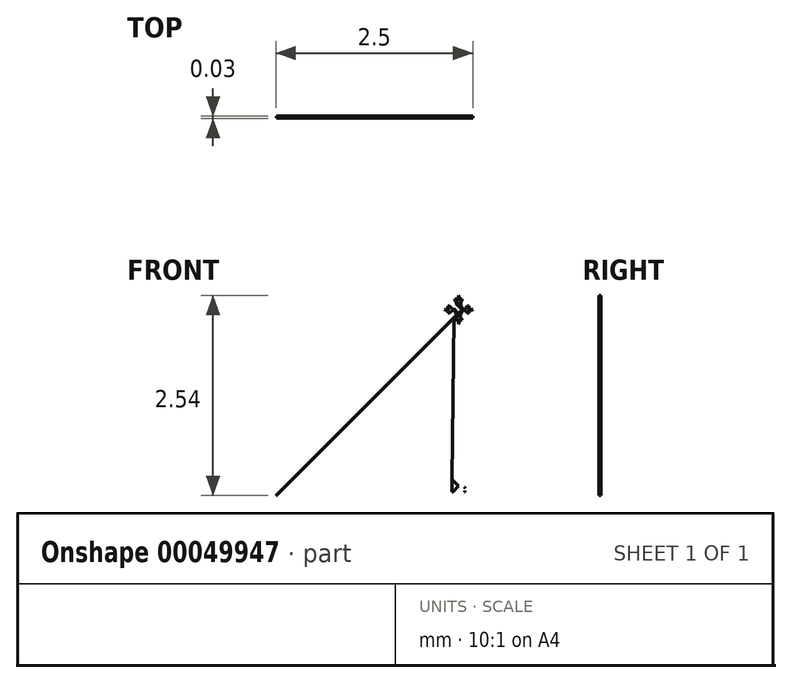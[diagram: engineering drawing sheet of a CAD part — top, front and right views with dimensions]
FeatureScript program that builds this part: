
annotation { "Feature Type Name" : "Feature", "Feature Type Description" : "" }
export const myFeature = defineFeature(function(context is Context, id is Id, definition is map)
    precondition{}
    {
        {
            var Q0;
            Q0=qCreatedBy(makeId("Front.planeOp"),FACE);
            var sketch = newSketch(context, id + "F0", { "sketchPlane" : qUnion([Q0])});
            skLineSegment(sketch, "E0", {"start": v(0, 0) * mm, "end": v(5.08, 0) * mm, "construction": true});
            skLineSegment(sketch, "E1", {"start": v(5.08, 0) * mm, "end": v(5.08, 5.08) * mm, "construction": true});
            skLineSegment(sketch, "E2", {"start": v(5.08, 5.08) * mm, "end": v(0, 5.08) * mm, "construction": true});
            skLineSegment(sketch, "E3", {"start": v(0, 5.08) * mm, "end": v(0, 0) * mm, "construction": true});
            skLineSegment(sketch, "E4", {"start": v(0, 2.54) * mm, "end": v(5.08, 2.54) * mm, "construction": true});
            skLineSegment(sketch, "E5", {"start": v(5.08, 2.54) * mm, "end": v(2.54, 5.08) * mm, "construction": true});
            skLineSegment(sketch, "E6", {"start": v(2.54, 5.08) * mm, "end": v(2.54, 0) * mm, "construction": true});
            skLineSegment(sketch, "E7", {"start": v(2.54, 0) * mm, "end": v(0, 2.54) * mm, "construction": true});
            skLineSegment(sketch, "E8", {"start": v(2.54, 5.08) * mm, "end": v(0, 2.54) * mm, "construction": true});
            skLineSegment(sketch, "E9", {"start": v(2.54, 0) * mm, "end": v(5.08, 2.54) * mm, "construction": true});
            skCircle(sketch, "E10.cCircle", {"center": v(2.54, 2.54) * mm, "radius": 0.05 * mm, "construction": true});
            skLineSegment(sketch, "E10.0", {"start": v(2.57, 2.49) * mm, "end": v(2.51, 2.49) * mm});
            skLineSegment(sketch, "E10.1", {"start": v(2.51, 2.49) * mm, "end": v(2.48, 2.54) * mm});
            skLineSegment(sketch, "E10.2", {"start": v(2.48, 2.54) * mm, "end": v(2.51, 2.6) * mm});
            skLineSegment(sketch, "E10.3", {"start": v(2.51, 2.6) * mm, "end": v(2.57, 2.6) * mm});
            skLineSegment(sketch, "E10.4", {"start": v(2.57, 2.6) * mm, "end": v(2.6, 2.54) * mm});
            skLineSegment(sketch, "E10.5", {"start": v(2.6, 2.54) * mm, "end": v(2.57, 2.49) * mm});
            skPoint(sketch, "E10.0.midPoint", {"position": v(2.54, 2.49) * mm});
            skLineSegment(sketch, "E11", {"start": v(2.54, 2.54) * mm, "end": v(2.6, 2.54) * mm});
            skLineSegment(sketch, "E12", {"start": v(2.54, 2.54) * mm, "end": v(2.54, 2.54) * mm});
            skLineSegment(sketch, "E13", {"start": v(5.08, 0.25) * mm, "end": v(5.08, 0.26) * mm});
            skLineSegment(sketch, "E14", {"start": v(0.26, 5.08) * mm, "end": v(0.25, 5.08) * mm});
            skLineSegment(sketch, "E15", {"start": v(0, 0.25) * mm, "end": v(0, 0.26) * mm});
            skLineSegment(sketch, "E16", {"start": v(0.26, 0) * mm, "end": v(0.25, 0) * mm});
            skLineSegment(sketch, "E17", {"start": v(2.51, 2.6) * mm, "end": v(2.51, 2.62) * mm, "construction": true});
            skLineSegment(sketch, "E18", {"start": v(2.51, 2.62) * mm, "end": v(2.54, 2.62) * mm, "construction": true});
            skLineSegment(sketch, "E19", {"start": v(2.54, 2.6) * mm, "end": v(2.51, 2.62) * mm});
            skLineSegment(sketch, "E20", {"start": v(2.51, 2.62) * mm, "end": v(2.52, 2.62) * mm});
            skLineSegment(sketch, "E21", {"start": v(2.51, 2.62) * mm, "end": v(2.51, 2.6) * mm});
            skLineSegment(sketch, "E22", {"start": v(2.52, 2.62) * mm, "end": v(2.54, 2.6) * mm});
            skLineSegment(sketch, "E23", {"start": v(2.51, 2.6) * mm, "end": v(2.53, 2.6) * mm});
            skLineSegment(sketch, "E24", {"start": v(2.57, 2.6) * mm, "end": v(2.57, 2.62) * mm, "construction": true});
            skLineSegment(sketch, "E25", {"start": v(2.57, 2.62) * mm, "end": v(0.26, 2.62) * mm, "construction": true});
            skLineSegment(sketch, "E26", {"start": v(2.57, 2.62) * mm, "end": v(2.54, 2.6) * mm});
            skLineSegment(sketch, "E27", {"start": v(2.57, 2.62) * mm, "end": v(2.56, 2.62) * mm});
            skLineSegment(sketch, "E28", {"start": v(2.57, 2.62) * mm, "end": v(2.57, 2.6) * mm});
            skLineSegment(sketch, "E29", {"start": v(2.54, 2.62) * mm, "end": v(2.54, 2.6) * mm});
            skLineSegment(sketch, "E30", {"start": v(2.57, 2.6) * mm, "end": v(2.56, 2.62) * mm});
            skLineSegment(sketch, "E31", {"start": v(2.56, 2.62) * mm, "end": v(2.54, 2.6) * mm});
            skLineSegment(sketch, "E32", {"start": v(2.57, 2.6) * mm, "end": v(2.55, 2.6) * mm});
            skLineSegment(sketch, "E33", {"start": v(0.22, 0.18) * mm, "end": v(0.25, 0.18) * mm, "construction": true});
            skLineSegment(sketch, "E34", {"start": v(2.57, 2.46) * mm, "end": v(2.54, 2.49) * mm});
            skLineSegment(sketch, "E35", {"start": v(2.54, 2.49) * mm, "end": v(0.22, 0.18) * mm});
            skLineSegment(sketch, "E36", {"start": v(0.22, 0.18) * mm, "end": v(0.22, 0.19) * mm});
            skLineSegment(sketch, "E37", {"start": v(0.22, 0.18) * mm, "end": v(0.23, 0.18) * mm});
            skLineSegment(sketch, "E38", {"start": v(0.23, 0.18) * mm, "end": v(0.22, 0.19) * mm});
            skLineSegment(sketch, "E39", {"start": v(0.22, 0.19) * mm, "end": v(2.53, 2.49) * mm});
            skLineSegment(sketch, "E40", {"start": v(0.23, 0.18) * mm, "end": v(0.25, 0.2) * mm});
            skLineSegment(sketch, "E41", {"start": v(2.57, 2.46) * mm, "end": v(2.57, 2.47) * mm});
            skLineSegment(sketch, "E42", {"start": v(2.57, 2.46) * mm, "end": v(2.56, 2.46) * mm});
            skLineSegment(sketch, "E43", {"start": v(2.56, 2.46) * mm, "end": v(2.54, 2.48) * mm});
            skLineSegment(sketch, "E44", {"start": v(2.57, 2.47) * mm, "end": v(2.55, 2.49) * mm});
            skLineSegment(sketch, "E45", {"start": v(2.54, 2.54) * mm, "end": v(2.5, 2.54) * mm});
            skCircle(sketch, "E46.cCircle", {"center": v(2.54, 2.54) * mm, "radius": 0.04 * mm, "construction": true});
            skLineSegment(sketch, "E46.0", {"start": v(2.5, 2.52) * mm, "end": v(2.5, 2.56) * mm});
            skLineSegment(sketch, "E46.1", {"start": v(2.5, 2.56) * mm, "end": v(2.54, 2.58) * mm});
            skLineSegment(sketch, "E46.2", {"start": v(2.54, 2.58) * mm, "end": v(2.58, 2.56) * mm});
            skLineSegment(sketch, "E46.3", {"start": v(2.58, 2.56) * mm, "end": v(2.58, 2.52) * mm});
            skLineSegment(sketch, "E46.4", {"start": v(2.58, 2.52) * mm, "end": v(2.54, 2.5) * mm});
            skLineSegment(sketch, "E46.5", {"start": v(2.54, 2.5) * mm, "end": v(2.5, 2.52) * mm});
            skPoint(sketch, "E46.0.midPoint", {"position": v(2.5, 2.54) * mm});
            skLineSegment(sketch, "E47", {"start": v(2.6, 0.26) * mm, "end": v(2.6, 2.54) * mm});
            skLineSegment(sketch, "E48", {"start": v(2.6, 0.26) * mm, "end": v(2.6, 0.25) * mm});
            skLineSegment(sketch, "E49", {"start": v(2.6, 0.25) * mm, "end": v(2.6, 0.22) * mm, "construction": true});
            skLineSegment(sketch, "E50", {"start": v(2.6, 0.22) * mm, "end": v(2.62, 0.22) * mm, "construction": true});
            skLineSegment(sketch, "E51", {"start": v(2.62, 0.22) * mm, "end": v(2.62, 0.25) * mm, "construction": true});
            skLineSegment(sketch, "E52", {"start": v(2.6, 0.25) * mm, "end": v(2.62, 0.22) * mm});
            skLineSegment(sketch, "E53", {"start": v(2.62, 0.22) * mm, "end": v(2.62, 0.23) * mm});
            skLineSegment(sketch, "E54", {"start": v(2.62, 0.22) * mm, "end": v(2.61, 0.22) * mm});
            skLineSegment(sketch, "E55", {"start": v(2.61, 0.22) * mm, "end": v(2.62, 0.23) * mm});
            skLineSegment(sketch, "E56", {"start": v(2.62, 0.23) * mm, "end": v(2.6, 0.25) * mm});
            skLineSegment(sketch, "E57", {"start": v(2.61, 0.22) * mm, "end": v(1.76, 1.08) * mm});
            skLineSegment(sketch, "E58", {"start": v(2.6, 0.26) * mm, "end": v(2.6, 0.28) * mm, "construction": true});
            skLineSegment(sketch, "E59", {"start": v(2.6, 0.28) * mm, "end": v(2.62, 0.28) * mm, "construction": true});
            skLineSegment(sketch, "E60", {"start": v(2.62, 0.28) * mm, "end": v(2.62, 0.26) * mm, "construction": true});
            skLineSegment(sketch, "E61", {"start": v(2.6, 0.26) * mm, "end": v(2.62, 0.28) * mm});
            skLineSegment(sketch, "E62", {"start": v(2.62, 0.27) * mm, "end": v(2.62, 0.28) * mm});
            skLineSegment(sketch, "E63", {"start": v(2.62, 0.28) * mm, "end": v(2.61, 0.28) * mm});
            skLineSegment(sketch, "E64", {"start": v(2.61, 0.28) * mm, "end": v(2.62, 0.27) * mm});
            skLineSegment(sketch, "E65", {"start": v(3.43, 1.1) * mm, "end": v(2.61, 0.28) * mm});
            skLineSegment(sketch, "E66", {"start": v(2.62, 0.27) * mm, "end": v(2.6, 0.26) * mm});
            skLineSegment(sketch, "E67", {"start": v(2.48, 2.54) * mm, "end": v(2.48, 2.54) * mm});
            skLineSegment(sketch, "E68", {"start": v(2.48, 0.28) * mm, "end": v(2.48, 2.54) * mm, "construction": true});
            skLineSegment(sketch, "E69", {"start": v(2.48, 0.28) * mm, "end": v(2.46, 0.28) * mm, "construction": true});
            skLineSegment(sketch, "E70", {"start": v(2.46, 0.28) * mm, "end": v(2.46, 0.26) * mm, "construction": true});
            skLineSegment(sketch, "E71", {"start": v(2.48, 2.54) * mm, "end": v(2.46, 0.28) * mm});
            skLineSegment(sketch, "E72", {"start": v(2.46, 0.28) * mm, "end": v(2.47, 0.28) * mm});
            skLineSegment(sketch, "E73", {"start": v(2.46, 0.28) * mm, "end": v(2.46, 0.27) * mm});
            skLineSegment(sketch, "E74", {"start": v(2.46, 0.27) * mm, "end": v(2.47, 0.28) * mm});
            skLineSegment(sketch, "E75", {"start": v(2.46, 0.27) * mm, "end": v(2.47, 0.26) * mm});
            skLineSegment(sketch, "E76", {"start": v(1.65, 1.1) * mm, "end": v(2.47, 0.28) * mm});
            skLineSegment(sketch, "E77", {"start": v(2.48, 2.54) * mm, "end": v(2.48, 0.22) * mm, "construction": true});
            skLineSegment(sketch, "E78", {"start": v(2.48, 0.22) * mm, "end": v(2.46, 0.22) * mm, "construction": true});
            skLineSegment(sketch, "E79", {"start": v(2.46, 0.22) * mm, "end": v(2.46, 0.25) * mm, "construction": true});
            skLineSegment(sketch, "E80", {"start": v(2.46, 0.22) * mm, "end": v(2.48, 2.54) * mm});
            skLineSegment(sketch, "E81", {"start": v(2.46, 0.22) * mm, "end": v(2.47, 0.22) * mm});
            skLineSegment(sketch, "E82", {"start": v(2.47, 0.22) * mm, "end": v(2.46, 0.23) * mm});
            skLineSegment(sketch, "E83", {"start": v(2.46, 0.23) * mm, "end": v(2.46, 0.22) * mm});
            skLineSegment(sketch, "E84", {"start": v(2.46, 0.23) * mm, "end": v(2.47, 0.25) * mm});
            skLineSegment(sketch, "E85", {"start": v(2.47, 0.22) * mm, "end": v(3.32, 1.08) * mm});
            skLineSegment(sketch, "E86", {"start": v(2.54, 2.54) * mm, "end": v(2.36, 2.54) * mm});
            skLineSegment(sketch, "E87", {"start": v(2.36, 2.54) * mm, "end": v(2.36, 2.54) * mm});
            skLineSegment(sketch, "E88", {"start": v(2.54, 2.54) * mm, "end": v(2.72, 2.54) * mm});
            skLineSegment(sketch, "E89", {"start": v(2.72, 2.54) * mm, "end": v(2.72, 2.54) * mm});
            skLineSegment(sketch, "E90", {"start": v(2.54, 2.54) * mm, "end": v(2.54, 2.72) * mm});
            skLineSegment(sketch, "E91", {"start": v(2.54, 2.72) * mm, "end": v(2.54, 2.72) * mm});
            skLineSegment(sketch, "E92", {"start": v(2.54, 2.54) * mm, "end": v(2.54, 2.36) * mm});
            skLineSegment(sketch, "E93", {"start": v(2.54, 2.36) * mm, "end": v(2.54, 2.36) * mm});
            skLineSegment(sketch, "E94", {"start": v(2.63, 2.54) * mm, "end": v(2.63, 2.58) * mm});
            skLineSegment(sketch, "E95", {"start": v(2.63, 2.58) * mm, "end": v(2.67, 2.58) * mm, "construction": true});
            skLineSegment(sketch, "E96", {"start": v(2.67, 2.58) * mm, "end": v(2.67, 2.54) * mm, "construction": true});
            skLineSegment(sketch, "E97", {"start": v(2.67, 2.58) * mm, "end": v(2.63, 2.54) * mm});
            skLineSegment(sketch, "E98", {"start": v(2.67, 2.58) * mm, "end": v(2.67, 2.56) * mm});
            skLineSegment(sketch, "E99", {"start": v(2.67, 2.56) * mm, "end": v(2.65, 2.58) * mm});
            skLineSegment(sketch, "E100", {"start": v(2.65, 2.58) * mm, "end": v(2.67, 2.58) * mm});
            skLineSegment(sketch, "E101", {"start": v(2.65, 2.58) * mm, "end": v(2.61, 2.54) * mm});
            skLineSegment(sketch, "E102", {"start": v(2.67, 2.56) * mm, "end": v(2.65, 2.54) * mm});
            skLineSegment(sketch, "E103", {"start": v(2.63, 2.54) * mm, "end": v(2.63, 2.5) * mm});
            skLineSegment(sketch, "E104", {"start": v(2.63, 2.5) * mm, "end": v(2.67, 2.5) * mm, "construction": true});
            skLineSegment(sketch, "E105", {"start": v(2.67, 2.5) * mm, "end": v(2.67, 2.54) * mm, "construction": true});
            skLineSegment(sketch, "E106", {"start": v(2.63, 2.54) * mm, "end": v(2.67, 2.5) * mm});
            skLineSegment(sketch, "E107", {"start": v(2.67, 2.52) * mm, "end": v(2.67, 2.5) * mm});
            skLineSegment(sketch, "E108", {"start": v(2.67, 2.52) * mm, "end": v(2.65, 2.5) * mm});
            skLineSegment(sketch, "E109", {"start": v(2.65, 2.5) * mm, "end": v(2.67, 2.5) * mm});
            skLineSegment(sketch, "E110", {"start": v(2.67, 2.52) * mm, "end": v(2.65, 2.54) * mm});
            skLineSegment(sketch, "E111", {"start": v(2.65, 2.5) * mm, "end": v(2.61, 2.54) * mm});
            skLineSegment(sketch, "E112", {"start": v(2.54, 2.45) * mm, "end": v(2.5, 2.45) * mm, "construction": true});
            skLineSegment(sketch, "E113", {"start": v(2.5, 2.45) * mm, "end": v(2.5, 2.4) * mm, "construction": true});
            skLineSegment(sketch, "E114", {"start": v(2.5, 2.4) * mm, "end": v(2.54, 2.4) * mm, "construction": true});
            skLineSegment(sketch, "E115", {"start": v(2.5, 2.4) * mm, "end": v(2.54, 2.45) * mm});
            skLineSegment(sketch, "E116", {"start": v(2.5, 2.4) * mm, "end": v(2.51, 2.4) * mm});
            skLineSegment(sketch, "E117", {"start": v(2.51, 2.4) * mm, "end": v(2.5, 2.42) * mm});
            skLineSegment(sketch, "E118", {"start": v(2.5, 2.42) * mm, "end": v(2.5, 2.4) * mm});
            skLineSegment(sketch, "E119", {"start": v(2.5, 2.42) * mm, "end": v(2.54, 2.46) * mm});
            skLineSegment(sketch, "E120", {"start": v(2.51, 2.4) * mm, "end": v(2.54, 2.43) * mm});
            skLineSegment(sketch, "E121", {"start": v(2.54, 2.45) * mm, "end": v(2.54, 2.45) * mm});
            skLineSegment(sketch, "E122", {"start": v(2.54, 2.45) * mm, "end": v(2.58, 2.45) * mm, "construction": true});
            skLineSegment(sketch, "E123", {"start": v(2.58, 2.45) * mm, "end": v(2.58, 2.4) * mm, "construction": true});
            skLineSegment(sketch, "E124", {"start": v(2.58, 2.4) * mm, "end": v(2.54, 2.4) * mm, "construction": true});
            skLineSegment(sketch, "E125", {"start": v(2.54, 2.45) * mm, "end": v(2.58, 2.4) * mm});
            skLineSegment(sketch, "E126", {"start": v(2.58, 2.42) * mm, "end": v(2.58, 2.4) * mm});
            skLineSegment(sketch, "E127", {"start": v(2.57, 2.4) * mm, "end": v(2.58, 2.4) * mm});
            skLineSegment(sketch, "E128", {"start": v(2.58, 2.42) * mm, "end": v(2.57, 2.4) * mm});
            skLineSegment(sketch, "E129", {"start": v(2.57, 2.4) * mm, "end": v(2.54, 2.43) * mm});
            skLineSegment(sketch, "E130", {"start": v(2.58, 2.42) * mm, "end": v(2.54, 2.46) * mm});
            skLineSegment(sketch, "E131", {"start": v(2.45, 2.54) * mm, "end": v(2.45, 2.58) * mm, "construction": true});
            skLineSegment(sketch, "E132", {"start": v(2.45, 2.58) * mm, "end": v(2.4, 2.58) * mm, "construction": true});
            skLineSegment(sketch, "E133", {"start": v(2.4, 2.58) * mm, "end": v(2.4, 2.54) * mm, "construction": true});
            skLineSegment(sketch, "E134", {"start": v(2.4, 2.58) * mm, "end": v(2.4, 2.56) * mm});
            skLineSegment(sketch, "E135", {"start": v(2.4, 2.58) * mm, "end": v(2.43, 2.58) * mm});
            skLineSegment(sketch, "E136", {"start": v(2.4, 2.56) * mm, "end": v(2.43, 2.58) * mm});
            skLineSegment(sketch, "E137", {"start": v(2.4, 2.56) * mm, "end": v(2.43, 2.54) * mm});
            skLineSegment(sketch, "E138", {"start": v(2.43, 2.58) * mm, "end": v(2.47, 2.54) * mm});
            skLineSegment(sketch, "E139", {"start": v(2.4, 2.58) * mm, "end": v(2.45, 2.54) * mm});
            skLineSegment(sketch, "E140", {"start": v(2.45, 2.54) * mm, "end": v(2.45, 2.54) * mm});
            skLineSegment(sketch, "E141", {"start": v(2.45, 2.54) * mm, "end": v(2.45, 2.5) * mm, "construction": true});
            skLineSegment(sketch, "E142", {"start": v(2.45, 2.5) * mm, "end": v(2.4, 2.5) * mm, "construction": true});
            skLineSegment(sketch, "E143", {"start": v(2.4, 2.5) * mm, "end": v(2.4, 2.54) * mm, "construction": true});
            skLineSegment(sketch, "E144", {"start": v(2.45, 2.54) * mm, "end": v(2.4, 2.5) * mm});
            skLineSegment(sketch, "E145", {"start": v(2.4, 2.5) * mm, "end": v(2.43, 2.5) * mm});
            skLineSegment(sketch, "E146", {"start": v(2.4, 2.5) * mm, "end": v(2.4, 2.52) * mm});
            skLineSegment(sketch, "E147", {"start": v(2.4, 2.52) * mm, "end": v(2.43, 2.5) * mm});
            skLineSegment(sketch, "E148", {"start": v(2.4, 2.52) * mm, "end": v(2.43, 2.54) * mm});
            skLineSegment(sketch, "E149", {"start": v(2.43, 2.5) * mm, "end": v(2.47, 2.54) * mm});
            skLineSegment(sketch, "E150", {"start": v(2.54, 2.63) * mm, "end": v(2.54, 2.63) * mm});
            skLineSegment(sketch, "E151", {"start": v(2.54, 2.63) * mm, "end": v(2.58, 2.63) * mm, "construction": true});
            skLineSegment(sketch, "E152", {"start": v(2.58, 2.63) * mm, "end": v(2.58, 2.67) * mm, "construction": true});
            skLineSegment(sketch, "E153", {"start": v(2.58, 2.67) * mm, "end": v(2.54, 2.67) * mm, "construction": true});
            skLineSegment(sketch, "E154", {"start": v(2.58, 2.67) * mm, "end": v(2.54, 2.63) * mm});
            skLineSegment(sketch, "E155", {"start": v(2.58, 2.67) * mm, "end": v(2.58, 2.65) * mm});
            skLineSegment(sketch, "E156", {"start": v(2.58, 2.67) * mm, "end": v(2.56, 2.67) * mm});
            skLineSegment(sketch, "E157", {"start": v(2.56, 2.67) * mm, "end": v(2.58, 2.65) * mm});
            skLineSegment(sketch, "E158", {"start": v(2.58, 2.65) * mm, "end": v(2.54, 2.61) * mm});
            skLineSegment(sketch, "E159", {"start": v(2.56, 2.67) * mm, "end": v(2.54, 2.65) * mm});
            skLineSegment(sketch, "E160", {"start": v(2.54, 2.63) * mm, "end": v(2.5, 2.63) * mm, "construction": true});
            skLineSegment(sketch, "E161", {"start": v(2.5, 2.63) * mm, "end": v(2.5, 2.67) * mm, "construction": true});
            skLineSegment(sketch, "E162", {"start": v(2.5, 2.67) * mm, "end": v(2.54, 2.67) * mm, "construction": true});
            skLineSegment(sketch, "E163", {"start": v(2.5, 2.67) * mm, "end": v(2.54, 2.63) * mm});
            skLineSegment(sketch, "E164", {"start": v(2.5, 2.67) * mm, "end": v(2.52, 2.67) * mm});
            skLineSegment(sketch, "E165", {"start": v(2.52, 2.67) * mm, "end": v(2.5, 2.65) * mm});
            skLineSegment(sketch, "E166", {"start": v(2.5, 2.65) * mm, "end": v(2.5, 2.67) * mm});
            skLineSegment(sketch, "E167", {"start": v(2.5, 2.65) * mm, "end": v(2.54, 2.61) * mm});
            skLineSegment(sketch, "E168", {"start": v(2.52, 2.67) * mm, "end": v(2.54, 2.65) * mm});
            skLineSegment(sketch, "E169", {"start": v(2.72, 2.54) * mm, "end": v(2.71, 2.54) * mm});
            skLineSegment(sketch, "E170", {"start": v(2.71, 2.54) * mm, "end": v(2.71, 2.54) * mm});
            skLineSegment(sketch, "E171", {"start": v(2.71, 2.54) * mm, "end": v(2.72, 2.54) * mm});
            skLineSegment(sketch, "E172", {"start": v(2.54, 2.36) * mm, "end": v(2.54, 2.37) * mm});
            skLineSegment(sketch, "E173", {"start": v(2.54, 2.37) * mm, "end": v(2.54, 2.37) * mm});
            skLineSegment(sketch, "E174", {"start": v(2.54, 2.37) * mm, "end": v(2.54, 2.36) * mm});
            skLineSegment(sketch, "E175", {"start": v(2.36, 2.54) * mm, "end": v(2.37, 2.54) * mm});
            skLineSegment(sketch, "E176", {"start": v(2.37, 2.54) * mm, "end": v(2.37, 2.54) * mm});
            skLineSegment(sketch, "E177", {"start": v(2.37, 2.54) * mm, "end": v(2.36, 2.54) * mm});
            skLineSegment(sketch, "E178", {"start": v(2.54, 2.72) * mm, "end": v(2.54, 2.71) * mm});
            skLineSegment(sketch, "E179", {"start": v(2.54, 2.71) * mm, "end": v(2.54, 2.71) * mm});
            skLineSegment(sketch, "E180", {"start": v(2.54, 2.71) * mm, "end": v(2.54, 2.72) * mm});
            skSolve(sketch);
        }
        {
            var Q0;
            {var subQ0=sQuery(id+"F0.wireOp",EDGE,"E34");Q0=makeQuery(id+"F0.imprint","IMPRINT",FACE,{"disambiguationData":[TD([[makeQuery(id+"F0.imprint","IMPRINT",EDGE,{"derivedFrom":subQ0}),-1.0]])]});}
            var Q1;
            {var subQ0=sQuery(id+"F0.wireOp",EDGE,"E19");Q1=makeQuery(id+"F0.imprint","IMPRINT",FACE,{"disambiguationData":[TD([[makeQuery(id+"F0.imprint","IMPRINT",EDGE,{"derivedFrom":subQ0}),1.0]])]});}
            var Q2;
            {var subQ0=sQuery(id+"F0.wireOp",EDGE,"E19");Q2=makeQuery(id+"F0.imprint","IMPRINT",FACE,{"disambiguationData":[TD([[makeQuery(id+"F0.imprint","IMPRINT",EDGE,{"derivedFrom":subQ0}),-1.0]])]});}
            var Q3;
            {var subQ0=sQuery(id+"F0.wireOp",EDGE,"E27");Q3=makeQuery(id+"F0.imprint","IMPRINT",FACE,{"disambiguationData":[TD([[makeQuery(id+"F0.imprint","IMPRINT",EDGE,{"derivedFrom":subQ0}),1.0]])]});}
            var Q4;
            {var subQ0=sQuery(id+"F0.wireOp",EDGE,"E28");Q4=makeQuery(id+"F0.imprint","IMPRINT",FACE,{"disambiguationData":[TD([[makeQuery(id+"F0.imprint","IMPRINT",EDGE,{"derivedFrom":subQ0}),-1.0]])]});}
            var Q5;
            {var subQ0=sQuery(id+"F0.wireOp",EDGE,"E34");Q5=makeQuery(id+"F0.imprint","IMPRINT",FACE,{"disambiguationData":[TD([[makeQuery(id+"F0.imprint","IMPRINT",EDGE,{"derivedFrom":subQ0}),1.0]])]});}
            var Q6;
            {var subQ0=sQuery(id+"F0.wireOp",EDGE,"E36");Q6=makeQuery(id+"F0.imprint","IMPRINT",FACE,{"disambiguationData":[TD([[makeQuery(id+"F0.imprint","IMPRINT",EDGE,{"derivedFrom":subQ0}),-1.0]])]});}
            var Q7;
            {var subQ0=sQuery(id+"F0.wireOp",EDGE,"E37");Q7=makeQuery(id+"F0.imprint","IMPRINT",FACE,{"disambiguationData":[TD([[makeQuery(id+"F0.imprint","IMPRINT",EDGE,{"derivedFrom":subQ0}),1.0]])]});}
            var Q8;
            {var subQ0=sQuery(id+"F0.wireOp",EDGE,"E53");Q8=makeQuery(id+"F0.imprint","IMPRINT",FACE,{"disambiguationData":[TD([[makeQuery(id+"F0.imprint","IMPRINT",EDGE,{"derivedFrom":subQ0}),1.0]])]});}
            var Q9;
            {var subQ0=sQuery(id+"F0.wireOp",EDGE,"E54");Q9=makeQuery(id+"F0.imprint","IMPRINT",FACE,{"disambiguationData":[TD([[makeQuery(id+"F0.imprint","IMPRINT",EDGE,{"derivedFrom":subQ0}),-1.0]])]});}
            var Q10;
            {var subQ0=sQuery(id+"F0.wireOp",EDGE,"E62");Q10=makeQuery(id+"F0.imprint","IMPRINT",FACE,{"disambiguationData":[TD([[makeQuery(id+"F0.imprint","IMPRINT",EDGE,{"derivedFrom":subQ0}),1.0]])]});}
            var Q11;
            {var subQ0=sQuery(id+"F0.wireOp",EDGE,"E63");Q11=makeQuery(id+"F0.imprint","IMPRINT",FACE,{"disambiguationData":[TD([[makeQuery(id+"F0.imprint","IMPRINT",EDGE,{"derivedFrom":subQ0}),1.0]])]});}
            var Q12;
            {var subQ0=sQuery(id+"F0.wireOp",EDGE,"E72");Q12=makeQuery(id+"F0.imprint","IMPRINT",FACE,{"disambiguationData":[TD([[makeQuery(id+"F0.imprint","IMPRINT",EDGE,{"derivedFrom":subQ0}),-1.0]])]});}
            var Q13;
            {var subQ0=sQuery(id+"F0.wireOp",EDGE,"E73");Q13=makeQuery(id+"F0.imprint","IMPRINT",FACE,{"disambiguationData":[TD([[makeQuery(id+"F0.imprint","IMPRINT",EDGE,{"derivedFrom":subQ0}),1.0]])]});}
            var Q14;
            {var subQ0=sQuery(id+"F0.wireOp",EDGE,"E81");Q14=makeQuery(id+"F0.imprint","IMPRINT",FACE,{"disambiguationData":[TD([[makeQuery(id+"F0.imprint","IMPRINT",EDGE,{"derivedFrom":subQ0}),1.0]])]});}
            var Q15;
            {var subQ0=sQuery(id+"F0.wireOp",EDGE,"E83");Q15=makeQuery(id+"F0.imprint","IMPRINT",FACE,{"disambiguationData":[TD([[makeQuery(id+"F0.imprint","IMPRINT",EDGE,{"derivedFrom":subQ0}),1.0]])]});}
            var Q16;
            {var subQ1=sQuery(id+"F0.wireOp",EDGE,"E88");var subQ3=sQuery(id+"F0.wireOp",EDGE,"E101");var subQ4=makeQuery(id+"F0.imprint","INTERSECT",VERTEX,{"derivedFrom":[subQ1,subQ3]});Q16=makeQuery(id+"F0.imprint","IMPRINT",FACE,{"disambiguationData":[TD([[makeQuery(id+"F0.imprint","IMPRINT",EDGE,{"disambiguationData":[TD([[subQ4,1.0]])],"derivedFrom":subQ3}),1.0]])]});}
            var Q17;
            {var subQ1=sQuery(id+"F0.wireOp",EDGE,"E88");var subQ3=sQuery(id+"F0.wireOp",EDGE,"E111");var subQ4=makeQuery(id+"F0.imprint","INTERSECT",VERTEX,{"derivedFrom":[subQ1,subQ3]});Q17=makeQuery(id+"F0.imprint","IMPRINT",FACE,{"disambiguationData":[TD([[makeQuery(id+"F0.imprint","IMPRINT",EDGE,{"disambiguationData":[TD([[subQ4,1.0]])],"derivedFrom":subQ3}),-1.0]])]});}
            var Q18;
            {var subQ0=sQuery(id+"F0.wireOp",EDGE,"E98");Q18=makeQuery(id+"F0.imprint","IMPRINT",FACE,{"disambiguationData":[TD([[makeQuery(id+"F0.imprint","IMPRINT",EDGE,{"derivedFrom":subQ0}),-1.0]])]});}
            var Q19;
            {var subQ0=sQuery(id+"F0.wireOp",EDGE,"E100");Q19=makeQuery(id+"F0.imprint","IMPRINT",FACE,{"disambiguationData":[TD([[makeQuery(id+"F0.imprint","IMPRINT",EDGE,{"derivedFrom":subQ0}),-1.0]])]});}
            var Q20;
            {var subQ0=sQuery(id+"F0.wireOp",EDGE,"E107");Q20=makeQuery(id+"F0.imprint","IMPRINT",FACE,{"disambiguationData":[TD([[makeQuery(id+"F0.imprint","IMPRINT",EDGE,{"derivedFrom":subQ0}),-1.0]])]});}
            var Q21;
            {var subQ0=sQuery(id+"F0.wireOp",EDGE,"E109");Q21=makeQuery(id+"F0.imprint","IMPRINT",FACE,{"disambiguationData":[TD([[makeQuery(id+"F0.imprint","IMPRINT",EDGE,{"derivedFrom":subQ0}),1.0]])]});}
            var Q22;
            {var subQ0=sQuery(id+"F0.wireOp",EDGE,"E116");Q22=makeQuery(id+"F0.imprint","IMPRINT",FACE,{"disambiguationData":[TD([[makeQuery(id+"F0.imprint","IMPRINT",EDGE,{"derivedFrom":subQ0}),1.0]])]});}
            var Q23;
            {var subQ0=sQuery(id+"F0.wireOp",EDGE,"E118");Q23=makeQuery(id+"F0.imprint","IMPRINT",FACE,{"disambiguationData":[TD([[makeQuery(id+"F0.imprint","IMPRINT",EDGE,{"derivedFrom":subQ0}),1.0]])]});}
            var Q24;
            {var subQ0=sQuery(id+"F0.wireOp",EDGE,"E126");Q24=makeQuery(id+"F0.imprint","IMPRINT",FACE,{"disambiguationData":[TD([[makeQuery(id+"F0.imprint","IMPRINT",EDGE,{"derivedFrom":subQ0}),-1.0]])]});}
            var Q25;
            {var subQ0=sQuery(id+"F0.wireOp",EDGE,"E127");Q25=makeQuery(id+"F0.imprint","IMPRINT",FACE,{"disambiguationData":[TD([[makeQuery(id+"F0.imprint","IMPRINT",EDGE,{"derivedFrom":subQ0}),1.0]])]});}
            var Q26;
            {var subQ0=sQuery(id+"F0.wireOp",EDGE,"E134");Q26=makeQuery(id+"F0.imprint","IMPRINT",FACE,{"disambiguationData":[TD([[makeQuery(id+"F0.imprint","IMPRINT",EDGE,{"derivedFrom":subQ0}),1.0]])]});}
            var Q27;
            {var subQ0=sQuery(id+"F0.wireOp",EDGE,"E135");Q27=makeQuery(id+"F0.imprint","IMPRINT",FACE,{"disambiguationData":[TD([[makeQuery(id+"F0.imprint","IMPRINT",EDGE,{"derivedFrom":subQ0}),-1.0]])]});}
            var Q28;
            {var subQ0=sQuery(id+"F0.wireOp",EDGE,"E145");Q28=makeQuery(id+"F0.imprint","IMPRINT",FACE,{"disambiguationData":[TD([[makeQuery(id+"F0.imprint","IMPRINT",EDGE,{"derivedFrom":subQ0}),1.0]])]});}
            var Q29;
            {var subQ0=sQuery(id+"F0.wireOp",EDGE,"E146");Q29=makeQuery(id+"F0.imprint","IMPRINT",FACE,{"disambiguationData":[TD([[makeQuery(id+"F0.imprint","IMPRINT",EDGE,{"derivedFrom":subQ0}),-1.0]])]});}
            var Q30;
            {var subQ0=sQuery(id+"F0.wireOp",EDGE,"E155");Q30=makeQuery(id+"F0.imprint","IMPRINT",FACE,{"disambiguationData":[TD([[makeQuery(id+"F0.imprint","IMPRINT",EDGE,{"derivedFrom":subQ0}),-1.0]])]});}
            var Q31;
            {var subQ0=sQuery(id+"F0.wireOp",EDGE,"E156");Q31=makeQuery(id+"F0.imprint","IMPRINT",FACE,{"disambiguationData":[TD([[makeQuery(id+"F0.imprint","IMPRINT",EDGE,{"derivedFrom":subQ0}),1.0]])]});}
            var Q32;
            {var subQ0=sQuery(id+"F0.wireOp",EDGE,"E164");Q32=makeQuery(id+"F0.imprint","IMPRINT",FACE,{"disambiguationData":[TD([[makeQuery(id+"F0.imprint","IMPRINT",EDGE,{"derivedFrom":subQ0}),-1.0]])]});}
            var Q33;
            {var subQ0=sQuery(id+"F0.wireOp",EDGE,"E166");Q33=makeQuery(id+"F0.imprint","IMPRINT",FACE,{"disambiguationData":[TD([[makeQuery(id+"F0.imprint","IMPRINT",EDGE,{"derivedFrom":subQ0}),-1.0]])]});}
            var Q34;
            {var subQ3=sQuery(id+"F0.wireOp",EDGE,"E39");Q34=makeQuery(id+"F0.imprint","IMPRINT",FACE,{"disambiguationData":[TD([[makeQuery(id+"F0.imprint","IMPRINT",EDGE,{"derivedFrom":subQ3}),-1.0]])]});}
            var Q35;
            {var subQ3=sQuery(id+"F0.wireOp",EDGE,"E32");Q35=makeQuery(id+"F0.imprint","IMPRINT",FACE,{"disambiguationData":[TD([[makeQuery(id+"F0.imprint","IMPRINT",EDGE,{"derivedFrom":subQ3}),-1.0]])]});}
            var Q36;
            {var subQ5=sQuery(id+"F0.wireOp",EDGE,"E31");Q36=makeQuery(id+"F0.imprint","IMPRINT",FACE,{"disambiguationData":[TD([[makeQuery(id+"F0.imprint","IMPRINT",EDGE,{"derivedFrom":subQ5}),1.0]])]});}
            var Q37;
            {var subQ5=sQuery(id+"F0.wireOp",EDGE,"E40");Q37=makeQuery(id+"F0.imprint","IMPRINT",FACE,{"disambiguationData":[TD([[makeQuery(id+"F0.imprint","IMPRINT",EDGE,{"derivedFrom":subQ5}),1.0]])]});}
            var Q38;
            {var subQ5=sQuery(id+"F0.wireOp",EDGE,"E56");Q38=makeQuery(id+"F0.imprint","IMPRINT",FACE,{"disambiguationData":[TD([[makeQuery(id+"F0.imprint","IMPRINT",EDGE,{"derivedFrom":subQ5}),1.0]])]});}
            var Q39;
            {var subQ5=sQuery(id+"F0.wireOp",EDGE,"E66");Q39=makeQuery(id+"F0.imprint","IMPRINT",FACE,{"disambiguationData":[TD([[makeQuery(id+"F0.imprint","IMPRINT",EDGE,{"derivedFrom":subQ5}),-1.0]])]});}
            var Q40;
            {var subQ5=sQuery(id+"F0.wireOp",EDGE,"E75");Q40=makeQuery(id+"F0.imprint","IMPRINT",FACE,{"disambiguationData":[TD([[makeQuery(id+"F0.imprint","IMPRINT",EDGE,{"derivedFrom":subQ5}),1.0]])]});}
            var Q41;
            {var subQ5=sQuery(id+"F0.wireOp",EDGE,"E84");Q41=makeQuery(id+"F0.imprint","IMPRINT",FACE,{"disambiguationData":[TD([[makeQuery(id+"F0.imprint","IMPRINT",EDGE,{"derivedFrom":subQ5}),-1.0]])]});}
            var Q42;
            {var subQ0=sQuery(id+"F0.wireOp",EDGE,"E138");Q42=makeQuery(id+"F0.imprint","IMPRINT",FACE,{"disambiguationData":[TD([[makeQuery(id+"F0.imprint","IMPRINT",EDGE,{"derivedFrom":subQ0}),-1.0]])]});}
            var Q43;
            {var subQ0=sQuery(id+"F0.wireOp",EDGE,"E137");Q43=makeQuery(id+"F0.imprint","IMPRINT",FACE,{"disambiguationData":[TD([[makeQuery(id+"F0.imprint","IMPRINT",EDGE,{"derivedFrom":subQ0}),1.0]])]});}
            var Q44;
            {var subQ3=sQuery(id+"F0.wireOp",EDGE,"E149");Q44=makeQuery(id+"F0.imprint","IMPRINT",FACE,{"disambiguationData":[TD([[makeQuery(id+"F0.imprint","IMPRINT",EDGE,{"derivedFrom":subQ3}),1.0]])]});}
            var Q45;
            {var subQ3=sQuery(id+"F0.wireOp",EDGE,"E148");Q45=makeQuery(id+"F0.imprint","IMPRINT",FACE,{"disambiguationData":[TD([[makeQuery(id+"F0.imprint","IMPRINT",EDGE,{"derivedFrom":subQ3}),-1.0]])]});}
            var Q46;
            {var subQ3=sQuery(id+"F0.wireOp",EDGE,"E102");Q46=makeQuery(id+"F0.imprint","IMPRINT",FACE,{"disambiguationData":[TD([[makeQuery(id+"F0.imprint","IMPRINT",EDGE,{"derivedFrom":subQ3}),-1.0]])]});}
            var Q47;
            {var subQ3=sQuery(id+"F0.wireOp",EDGE,"E110");Q47=makeQuery(id+"F0.imprint","IMPRINT",FACE,{"disambiguationData":[TD([[makeQuery(id+"F0.imprint","IMPRINT",EDGE,{"derivedFrom":subQ3}),1.0]])]});}
            var Q48;
            {var subQ3=sQuery(id+"F0.wireOp",EDGE,"E158");Q48=makeQuery(id+"F0.imprint","IMPRINT",FACE,{"disambiguationData":[TD([[makeQuery(id+"F0.imprint","IMPRINT",EDGE,{"derivedFrom":subQ3}),-1.0]])]});}
            var Q49;
            {var subQ3=sQuery(id+"F0.wireOp",EDGE,"E159");Q49=makeQuery(id+"F0.imprint","IMPRINT",FACE,{"disambiguationData":[TD([[makeQuery(id+"F0.imprint","IMPRINT",EDGE,{"derivedFrom":subQ3}),1.0]])]});}
            var Q50;
            {var subQ0=sQuery(id+"F0.wireOp",EDGE,"E167");Q50=makeQuery(id+"F0.imprint","IMPRINT",FACE,{"disambiguationData":[TD([[makeQuery(id+"F0.imprint","IMPRINT",EDGE,{"derivedFrom":subQ0}),1.0]])]});}
            var Q51;
            {var subQ3=sQuery(id+"F0.wireOp",EDGE,"E168");Q51=makeQuery(id+"F0.imprint","IMPRINT",FACE,{"disambiguationData":[TD([[makeQuery(id+"F0.imprint","IMPRINT",EDGE,{"derivedFrom":subQ3}),-1.0]])]});}
            var Q52;
            {var subQ3=sQuery(id+"F0.wireOp",EDGE,"E119");Q52=makeQuery(id+"F0.imprint","IMPRINT",FACE,{"disambiguationData":[TD([[makeQuery(id+"F0.imprint","IMPRINT",EDGE,{"derivedFrom":subQ3}),-1.0]])]});}
            var Q53;
            {var subQ3=sQuery(id+"F0.wireOp",EDGE,"E120");Q53=makeQuery(id+"F0.imprint","IMPRINT",FACE,{"disambiguationData":[TD([[makeQuery(id+"F0.imprint","IMPRINT",EDGE,{"derivedFrom":subQ3}),1.0]])]});}
            var Q54;
            {var subQ3=sQuery(id+"F0.wireOp",EDGE,"E130");Q54=makeQuery(id+"F0.imprint","IMPRINT",FACE,{"disambiguationData":[TD([[makeQuery(id+"F0.imprint","IMPRINT",EDGE,{"derivedFrom":subQ3}),1.0]])]});}
            var Q55;
            {var subQ3=sQuery(id+"F0.wireOp",EDGE,"E129");Q55=makeQuery(id+"F0.imprint","IMPRINT",FACE,{"disambiguationData":[TD([[makeQuery(id+"F0.imprint","IMPRINT",EDGE,{"derivedFrom":subQ3}),-1.0]])]});}
            var Q56;
            {var subQ1=sQuery(id+"F0.wireOp",EDGE,"E94");var subQ3=sQuery(id+"F0.wireOp",EDGE,"E101");var subQ4=makeQuery(id+"F0.imprint","INTERSECT",VERTEX,{"derivedFrom":[subQ1,subQ3]});Q56=makeQuery(id+"F0.imprint","IMPRINT",FACE,{"disambiguationData":[TD([[makeQuery(id+"F0.imprint","IMPRINT",EDGE,{"disambiguationData":[TD([[subQ4,1.0]])],"derivedFrom":subQ1}),-1.0]])]});}
            var Q57;
            {var subQ1=sQuery(id+"F0.wireOp",EDGE,"E103");var subQ3=sQuery(id+"F0.wireOp",EDGE,"E111");var subQ4=makeQuery(id+"F0.imprint","INTERSECT",VERTEX,{"derivedFrom":[subQ1,subQ3]});Q57=makeQuery(id+"F0.imprint","IMPRINT",FACE,{"disambiguationData":[TD([[makeQuery(id+"F0.imprint","IMPRINT",EDGE,{"disambiguationData":[TD([[subQ4,1.0]])],"derivedFrom":subQ1}),1.0]])]});}
            var Q58;
            {var subQ0=sQuery(id+"F0.wireOp",EDGE,"E169");Q58=makeQuery(id+"F0.imprint","IMPRINT",FACE,{"disambiguationData":[TD([[makeQuery(id+"F0.imprint","IMPRINT",EDGE,{"derivedFrom":subQ0}),1.0]])]});}
            var Q59;
            {var subQ0=sQuery(id+"F0.wireOp",EDGE,"E169");Q59=makeQuery(id+"F0.imprint","IMPRINT",FACE,{"disambiguationData":[TD([[makeQuery(id+"F0.imprint","IMPRINT",EDGE,{"derivedFrom":subQ0}),-1.0]])]});}
            var Q60;
            {var subQ0=sQuery(id+"F0.wireOp",EDGE,"E172");Q60=makeQuery(id+"F0.imprint","IMPRINT",FACE,{"disambiguationData":[TD([[makeQuery(id+"F0.imprint","IMPRINT",EDGE,{"derivedFrom":subQ0}),-1.0]])]});}
            var Q61;
            {var subQ0=sQuery(id+"F0.wireOp",EDGE,"E172");Q61=makeQuery(id+"F0.imprint","IMPRINT",FACE,{"disambiguationData":[TD([[makeQuery(id+"F0.imprint","IMPRINT",EDGE,{"derivedFrom":subQ0}),1.0]])]});}
            var Q62;
            {var subQ0=sQuery(id+"F0.wireOp",EDGE,"E175");Q62=makeQuery(id+"F0.imprint","IMPRINT",FACE,{"disambiguationData":[TD([[makeQuery(id+"F0.imprint","IMPRINT",EDGE,{"derivedFrom":subQ0}),1.0]])]});}
            var Q63;
            {var subQ0=sQuery(id+"F0.wireOp",EDGE,"E175");Q63=makeQuery(id+"F0.imprint","IMPRINT",FACE,{"disambiguationData":[TD([[makeQuery(id+"F0.imprint","IMPRINT",EDGE,{"derivedFrom":subQ0}),-1.0]])]});}
            var Q64;
            {var subQ0=sQuery(id+"F0.wireOp",EDGE,"E178");Q64=makeQuery(id+"F0.imprint","IMPRINT",FACE,{"disambiguationData":[TD([[makeQuery(id+"F0.imprint","IMPRINT",EDGE,{"derivedFrom":subQ0}),1.0]])]});}
            var Q65;
            {var subQ0=sQuery(id+"F0.wireOp",EDGE,"E178");Q65=makeQuery(id+"F0.imprint","IMPRINT",FACE,{"disambiguationData":[TD([[makeQuery(id+"F0.imprint","IMPRINT",EDGE,{"derivedFrom":subQ0}),-1.0]])]});}
            var Q66;
            {var subQ0=sQuery(id+"F0.wireOp",EDGE,"E85");Q66=makeQuery(id+"F0.imprint","IMPRINT",FACE,{"disambiguationData":[TD([[makeQuery(id+"F0.imprint","IMPRINT",EDGE,{"derivedFrom":subQ0}),1.0]])]});}
            var Q67;
            {var subQ0=sQuery(id+"F0.wireOp",EDGE,"E76");Q67=makeQuery(id+"F0.imprint","IMPRINT",FACE,{"disambiguationData":[TD([[makeQuery(id+"F0.imprint","IMPRINT",EDGE,{"derivedFrom":subQ0}),-1.0]])]});}
            var Q68;
            {var subQ0=sQuery(id+"F0.wireOp",EDGE,"E65");Q68=makeQuery(id+"F0.imprint","IMPRINT",FACE,{"disambiguationData":[TD([[makeQuery(id+"F0.imprint","IMPRINT",EDGE,{"derivedFrom":subQ0}),1.0]])]});}
            var Q69;
            {var subQ0=sQuery(id+"F0.wireOp",EDGE,"E57");Q69=makeQuery(id+"F0.imprint","IMPRINT",FACE,{"disambiguationData":[TD([[makeQuery(id+"F0.imprint","IMPRINT",EDGE,{"derivedFrom":subQ0}),-1.0]])]});}
            var Q70;
            {var subQ0=sQuery(id+"F0.wireOp",EDGE,"E10.5");var subQ1=sQuery(id+"F0.wireOp",EDGE,"E10.0");var subQ2=makeQuery(id+"F0.imprint","INTERSECT",VERTEX,{"derivedFrom":[subQ1,subQ0]});Q70=makeQuery(id+"F0.imprint","IMPRINT",FACE,{"disambiguationData":[TD([[makeQuery(id+"F0.imprint","IMPRINT",EDGE,{"disambiguationData":[TD([[subQ2,-1.0]])],"derivedFrom":subQ1}),-1.0]])]});}
            var Q71;
            {var subQ0=sQuery(id+"F0.wireOp",EDGE,"E10.1");var subQ4=sQuery(id+"F0.wireOp",EDGE,"E10.0");var subQ5=makeQuery(id+"F0.imprint","INTERSECT",VERTEX,{"derivedFrom":[subQ4,subQ0]});Q71=makeQuery(id+"F0.imprint","IMPRINT",FACE,{"disambiguationData":[TD([[makeQuery(id+"F0.imprint","IMPRINT",EDGE,{"disambiguationData":[TD([[subQ5,1.0]])],"derivedFrom":subQ4}),-1.0]])]});}
            var Q72;
            {var subQ4=sQuery(id+"F0.wireOp",EDGE,"E10.2");var subQ6=makeQuery(id+"F0.imprint","INTERSECT",VERTEX,{"derivedFrom":[subQ4,sQuery(id+"F0.wireOp",EDGE,"E76")]});Q72=makeQuery(id+"F0.imprint","IMPRINT",FACE,{"disambiguationData":[TD([[makeQuery(id+"F0.imprint","IMPRINT",EDGE,{"disambiguationData":[TD([[subQ6,1.0]])],"derivedFrom":subQ4}),-1.0]])]});}
            var Q73;
            {var subQ0=sQuery(id+"F0.wireOp",EDGE,"E10.4");var subQ4=sQuery(id+"F0.wireOp",EDGE,"E10.3");var subQ5=makeQuery(id+"F0.imprint","INTERSECT",VERTEX,{"derivedFrom":[subQ4,subQ0]});Q73=makeQuery(id+"F0.imprint","IMPRINT",FACE,{"disambiguationData":[TD([[makeQuery(id+"F0.imprint","IMPRINT",EDGE,{"disambiguationData":[TD([[subQ5,1.0]])],"derivedFrom":subQ4}),-1.0]])]});}
            var Q74;
            {var subQ4=sQuery(id+"F0.wireOp",EDGE,"E140");Q74=makeQuery(id+"F0.imprint","IMPRINT",FACE,{"disambiguationData":[TD([[makeQuery(id+"F0.imprint","IMPRINT",EDGE,{"derivedFrom":subQ4}),-1.0]])]});}
            var Q75;
            {var subQ4=sQuery(id+"F0.wireOp",EDGE,"E150");Q75=makeQuery(id+"F0.imprint","IMPRINT",FACE,{"disambiguationData":[TD([[makeQuery(id+"F0.imprint","IMPRINT",EDGE,{"derivedFrom":subQ4}),-1.0]])]});}
            var Q76;
            {var subQ0=sQuery(id+"F0.wireOp",EDGE,"E121");Q76=makeQuery(id+"F0.imprint","IMPRINT",FACE,{"disambiguationData":[TD([[makeQuery(id+"F0.imprint","IMPRINT",EDGE,{"derivedFrom":subQ0}),-1.0]])]});}
            var Q77;
            {var subQ0=sQuery(id+"F0.wireOp",EDGE,"E121");Q77=makeQuery(id+"F0.imprint","IMPRINT",FACE,{"disambiguationData":[TD([[makeQuery(id+"F0.imprint","IMPRINT",EDGE,{"derivedFrom":subQ0}),1.0]])]});}
            var Q78;
            {var subQ0=sQuery(id+"F0.wireOp",EDGE,"E150");Q78=makeQuery(id+"F0.imprint","IMPRINT",FACE,{"disambiguationData":[TD([[makeQuery(id+"F0.imprint","IMPRINT",EDGE,{"derivedFrom":subQ0}),1.0]])]});}
            var Q79;
            {var subQ10=sQuery(id+"F0.wireOp",EDGE,"E140");Q79=makeQuery(id+"F0.imprint","IMPRINT",FACE,{"disambiguationData":[TD([[makeQuery(id+"F0.imprint","IMPRINT",EDGE,{"derivedFrom":subQ10}),1.0]])]});}
            var Q80;
            {var subQ4=sQuery(id+"F0.wireOp",EDGE,"E88");var subQ17=makeQuery(id+"F0.imprint","INTERSECT",VERTEX,{"derivedFrom":[sQuery(id+"F0.wireOp",EDGE,"E66"),subQ4]});Q80=makeQuery(id+"F0.imprint","IMPRINT",FACE,{"disambiguationData":[TD([[makeQuery(id+"F0.imprint","IMPRINT",EDGE,{"disambiguationData":[TD([[subQ17,-1.0]])],"derivedFrom":subQ4}),-1.0]])]});}
            extrude(context, id + "F1", {"entities" : qUnion([Q0, Q1, Q2, Q3, Q4, Q5, Q6, Q7, Q8, Q9, Q10, Q11, Q12, Q13, Q14, Q15, Q16, Q17, Q18, Q19, Q20, Q21, Q22, Q23, Q24, Q25, Q26, Q27, Q28, Q29, Q30, Q31, Q32, Q33, Q34, Q35, Q36, Q37, Q38, Q39, Q40, Q41, Q42, Q43, Q44, Q45, Q46, Q47, Q48, Q49, Q50, Q51, Q52, Q53, Q54, Q55, Q56, Q57, Q58, Q59, Q60, Q61, Q62, Q63, Q64, Q65, Q66, Q67, Q68, Q69, Q70, Q71, Q72, Q73, Q74, Q75, Q76, Q77, Q78, Q79, Q80]), "depth" : 0.03 * mm});
        }
    });
